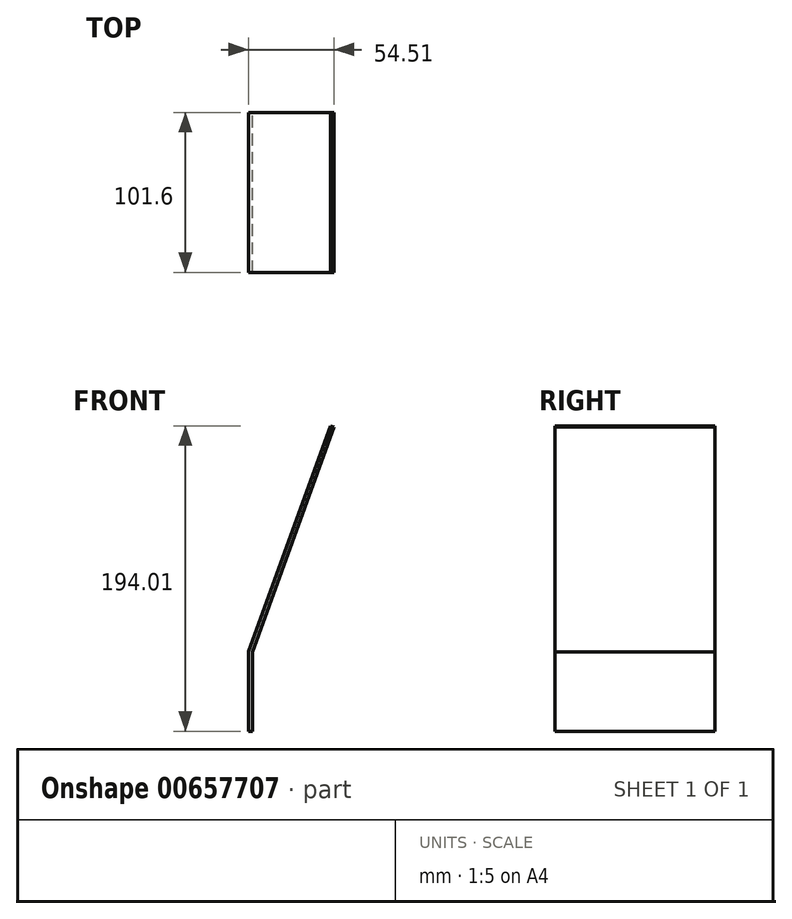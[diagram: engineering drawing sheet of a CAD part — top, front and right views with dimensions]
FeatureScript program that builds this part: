
annotation { "Feature Type Name" : "Feature", "Feature Type Description" : "" }
export const myFeature = defineFeature(function(context is Context, id is Id, definition is map)
    precondition{}
    {
        {
            var Q0;
            Q0=qCreatedBy(makeId("Front.planeOp"),FACE);
            var sketch = newSketch(context, id + "F0", { "sketchPlane" : qUnion([Q0])});
            skLineSegment(sketch, "E0", {"start": v(0, 0) * mm, "end": v(0, -50.8) * mm});
            skLineSegment(sketch, "E1", {"start": v(0, -50.8) * mm, "end": v(2.54, -50.8) * mm});
            skLineSegment(sketch, "E2", {"start": v(0, 0) * mm, "end": v(52.12, 143.2) * mm});
            skLineSegment(sketch, "E3", {"start": v(0, 0) * mm, "end": v(25.01, -4.41) * mm});
            skLineSegment(sketch, "E4", {"start": v(2.54, -50.8) * mm, "end": v(2.54, -0.45) * mm});
            skLineSegment(sketch, "E5", {"start": v(52.12, 143.2) * mm, "end": v(54.51, 142.34) * mm});
            skLineSegment(sketch, "E6", {"start": v(54.51, 142.34) * mm, "end": v(2.54, -0.45) * mm});
            skSolve(sketch);
        }
        {
            var Q0;
            {var subQ0=sQuery(id+"F0.wireOp",EDGE,"E2");Q0=makeQuery(id+"F0.imprint","IMPRINT",FACE,{"disambiguationData":[TD([[makeQuery(id+"F0.imprint","IMPRINT",EDGE,{"derivedFrom":subQ0}),-1.0]])]});}
            var Q1;
            {var subQ0=sQuery(id+"F0.wireOp",EDGE,"E0");Q1=makeQuery(id+"F0.imprint","IMPRINT",FACE,{"disambiguationData":[TD([[makeQuery(id+"F0.imprint","IMPRINT",EDGE,{"derivedFrom":subQ0}),1.0]])]});}
            extrude(context, id + "F1", {"entities" : qUnion([Q0, Q1]), "depth" : 101.6 * mm, "offsetDistance" : 25.4 * mm});
        }
    });
